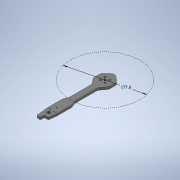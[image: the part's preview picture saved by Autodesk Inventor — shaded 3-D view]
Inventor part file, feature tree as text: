
AUTODESK INVENTOR PART (.ipt)
format: ipt  version: 2020 (Build 240168000, 168)  size: 248,832 bytes
history: native  units: in
note: dims shown in document units (in); Inventor stores cm internally (conversion verified against a paired STEP export)
features: sketch x3, fillet x2, extrude x1, projected_geometry x1
ambient origin geometry x8: Origin, YZ Plane, XZ Plane, XY Plane, X Axis, Y Axis, Z Axis, Center Point
bodies: Solid2 (feature_tree), Solid1 (feature_tree)
feature tree (7):
  sketch  "Sketch1"  dims[d0=7.0in d1=5.72in d2=0.8352in d3=0.2953in]
  sketch  "Sketch2"  dims[d4=0.2953in]
  extrude  "Extrusion1"  Depth=5.72in
  fillet  "Fillet2"  Radius=0.8352in
  fillet  "Fillet3"  Radius=0.2953in
  projected_geometry  "Projected Loop1"
  sketch  "Sketch3"  dims[d5=0.9835in d6=0.9835in d7=0.3937in d8=0.0in d10=0.3937in d11=0.7874in]
